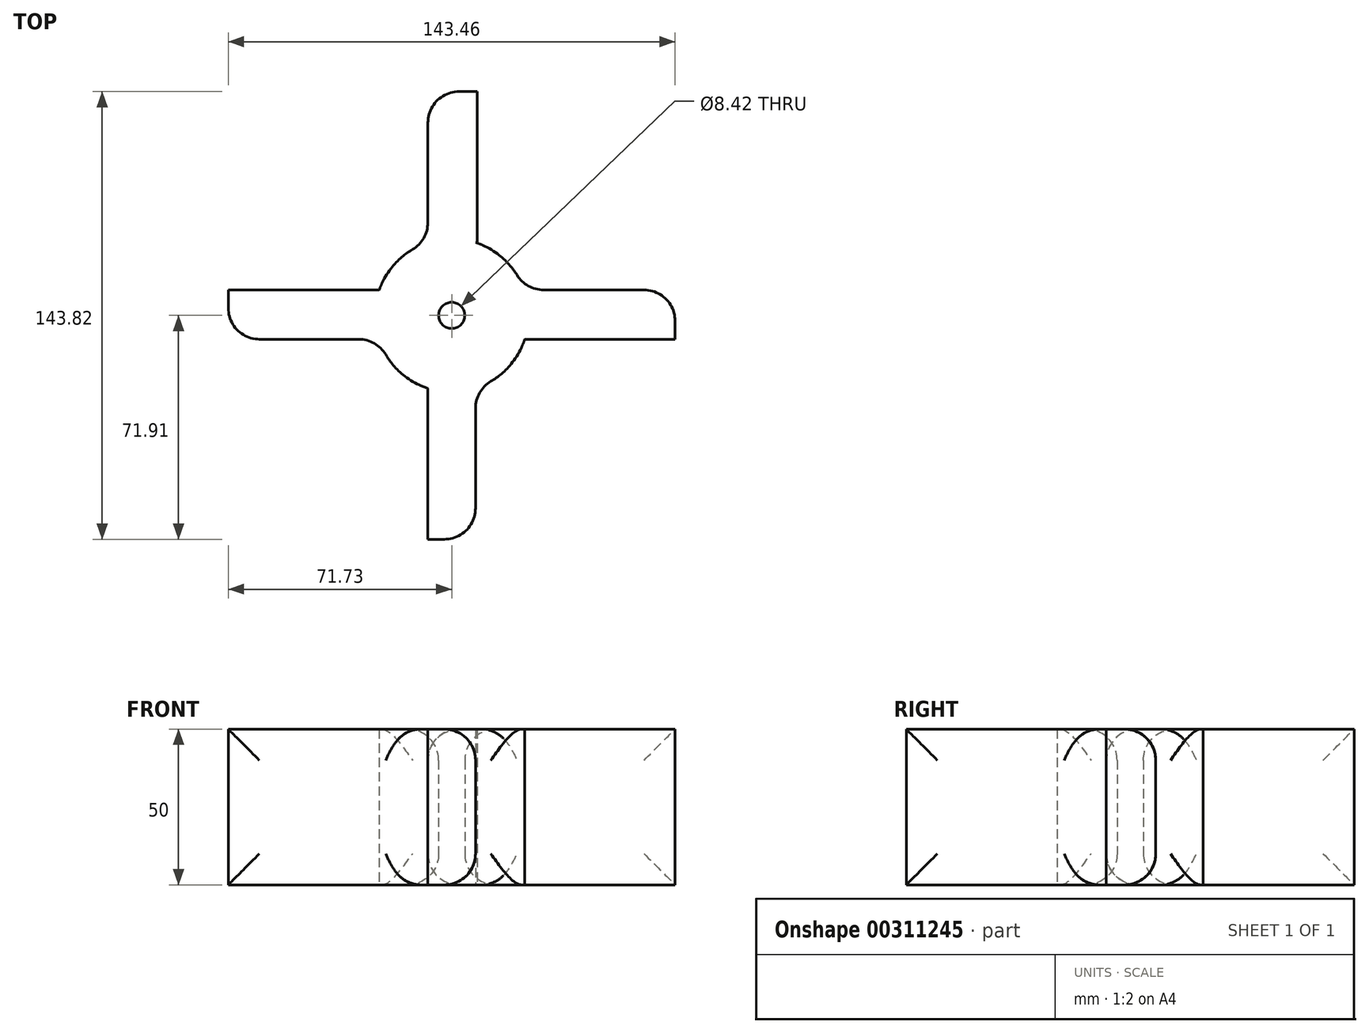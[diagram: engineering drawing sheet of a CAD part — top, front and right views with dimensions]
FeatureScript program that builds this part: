
annotation { "Feature Type Name" : "Feature", "Feature Type Description" : "" }
export const myFeature = defineFeature(function(context is Context, id is Id, definition is map)
    precondition{}
    {
        {
            var Q0;
            Q0=qCreatedBy(makeId("Top.planeOp"),FACE);
            var sketch = newSketch(context, id + "F0", { "sketchPlane" : qUnion([Q0])});
            skArc(sketch, "E0", {"start": v(7.66, -23.43) * mm, "mid": v(17.42, -17.43) * mm, "end": v(23.42, -7.67) * mm});
            skLineSegment(sketch, "E1.bottom", {"start": v(7.66, 23.43) * mm, "end": v(8.2, 23.43) * mm});
            skLineSegment(sketch, "E1.top", {"start": v(-7.66, 71.9) * mm, "end": v(8.2, 71.9) * mm});
            skLineSegment(sketch, "E1.left", {"start": v(-7.66, 23.43) * mm, "end": v(-7.66, 71.9) * mm});
            skLineSegment(sketch, "E1.right", {"start": v(8.2, 23.43) * mm, "end": v(8.2, 71.9) * mm});
            skLineSegment(sketch, "E2.bottom", {"start": v(-23.25, 8.2) * mm, "end": v(-71.73, 8.2) * mm});
            skLineSegment(sketch, "E2.top", {"start": v(-23.25, -7.67) * mm, "end": v(-71.73, -7.67) * mm});
            skLineSegment(sketch, "E2.right", {"start": v(-71.73, 8.2) * mm, "end": v(-71.73, -7.67) * mm});
            skLineSegment(sketch, "E3.MirrorCS", {"start": v(7.66, 23.43) * mm, "end": v(7.66, 71.9) * mm});
            skLineSegment(sketch, "E4.MirrorCS", {"start": v(7.66, 71.9) * mm, "end": v(-8.2, 71.9) * mm});
            skLineSegment(sketch, "E5.MirrorCS", {"start": v(23.25, 8.2) * mm, "end": v(71.73, 8.2) * mm});
            skLineSegment(sketch, "E6.MirrorCS", {"start": v(71.73, 8.2) * mm, "end": v(71.73, -7.67) * mm});
            skLineSegment(sketch, "E7.MirrorCS", {"start": v(23.25, -7.67) * mm, "end": v(71.73, -7.67) * mm});
            skArc(sketch, "E8.MirrorC", {"start": v(-7.66, -23.43) * mm, "mid": v(-17.42, -17.43) * mm, "end": v(-23.42, -7.67) * mm});
            skLineSegment(sketch, "E9.MirrorCS", {"start": v(7.66, -23.43) * mm, "end": v(8.2, -23.43) * mm});
            skLineSegment(sketch, "E10.MirrorCS", {"start": v(-7.66, -23.43) * mm, "end": v(-7.66, -71.9) * mm});
            skLineSegment(sketch, "E11.MirrorCS", {"start": v(7.66, -23.43) * mm, "end": v(7.66, -71.9) * mm});
            skLineSegment(sketch, "E12.MirrorCS", {"start": v(7.66, -71.9) * mm, "end": v(-8.2, -71.9) * mm});
            skCircle(sketch, "E13", {"center": v(0, 0) * mm, "radius": 4.21 * mm});
            skPoint(sketch, "E14.MirrorCS.end.orphan", {"position": v(23.25, -7.67) * mm});
            skPoint(sketch, "E14.MirrorCS.start.orphan", {"position": v(23.25, 8.2) * mm});
            skPoint(sketch, "E15.orphan", {"position": v(-7.66, -23.43) * mm});
            skArc(sketch, "E16.trimOffspring", {"start": v(23.25, 8.2) * mm, "mid": v(17.23, 17.63) * mm, "end": v(7.66, 23.43) * mm});
            skArc(sketch, "E17.trimOffspring", {"start": v(23.42, -7.67) * mm, "mid": v(17.42, -17.43) * mm, "end": v(7.66, -23.43) * mm});
            skArc(sketch, "E18.trimOffspring", {"start": v(7.66, 23.43) * mm, "mid": v(17.23, 17.63) * mm, "end": v(23.25, 8.2) * mm});
            skArc(sketch, "E19.trimOffspring", {"start": v(-23.25, 8.2) * mm, "mid": v(-17.23, 17.63) * mm, "end": v(-7.66, 23.43) * mm});
            skArc(sketch, "E20.trimOffspring", {"start": v(-23.42, -7.67) * mm, "mid": v(-17.42, -17.43) * mm, "end": v(-7.66, -23.43) * mm});
            skArc(sketch, "E21.trimOffspring", {"start": v(-7.66, 23.43) * mm, "mid": v(-17.23, 17.63) * mm, "end": v(-23.25, 8.2) * mm});
            skSolve(sketch);
        }
        {
            var Q0;
            Q0 = qSketchRegion(id + "F0", true);
            extrude(context, id + "F1", {"entities" : qUnion([Q0]), "endBound" : BoundingType.SYMMETRIC, "depth" : 50 * mm});
        }
        {
            var Q0;
            Q0=makeQuery(id+"F1.opExtrude","CAP_EDGE",EDGE,{"disambiguationData":[OSD([sQuery(id+"F0.wireOp",EDGE,"E13")])],"isStart":true});
            var Q1;
            Q1=makeQuery(id+"F1.opExtrude","CAP_EDGE",EDGE,{"disambiguationData":[OSD([sQuery(id+"F0.wireOp",EDGE,"E13")])],"isStart":false});
            var Q2;
            Q2=makeQuery(id+"F1.opExtrude","SWEPT_FACE",FACE,{"disambiguationData":[OSD([sQuery(id+"F0.wireOp",EDGE,"E1.left")])]});
            var Q3;
            Q3=makeQuery(id+"F1.opExtrude","SWEPT_FACE",FACE,{"disambiguationData":[OSD([sQuery(id+"F0.wireOp",EDGE,"E5.MirrorCS")])]});
            var Q4;
            Q4=makeQuery(id+"F1.opExtrude","SWEPT_FACE",FACE,{"disambiguationData":[OSD([sQuery(id+"F0.wireOp",EDGE,"E11.MirrorCS")])]});
            var Q5;
            Q5=makeQuery(id+"F1.opExtrude","SWEPT_FACE",FACE,{"disambiguationData":[OSD([sQuery(id+"F0.wireOp",EDGE,"E2.top")])]});
            fillet(context, id + "F2", {"entities" : qUnion([Q0, Q1, Q2, Q3, Q4, Q5]), "radius" : 10 * mm, "allowEdgeOverflow" : false});
        }
    });
